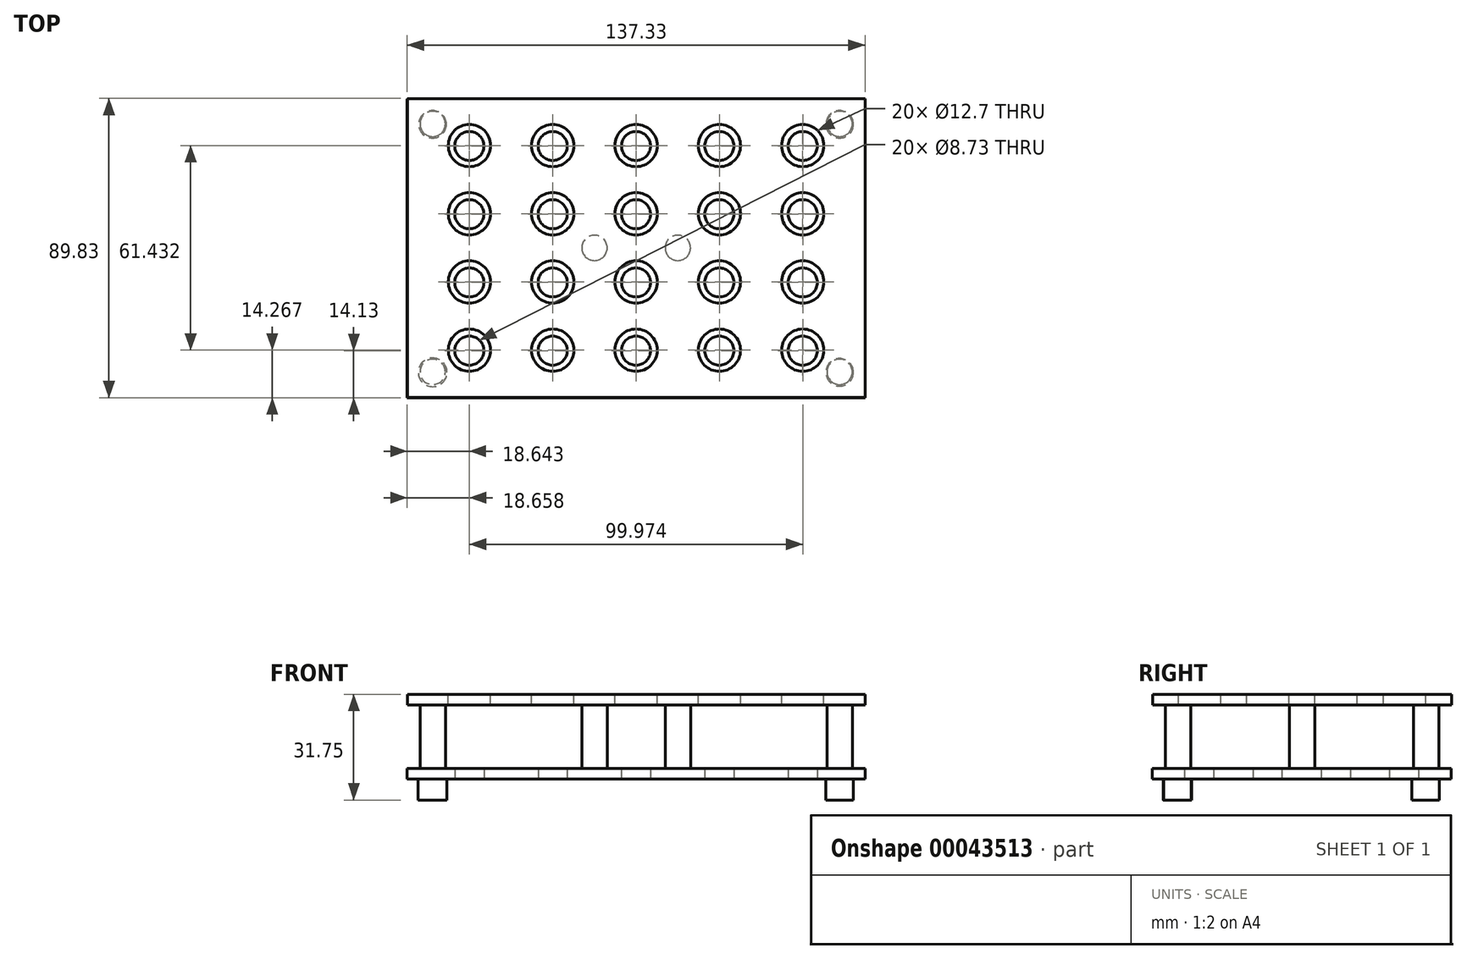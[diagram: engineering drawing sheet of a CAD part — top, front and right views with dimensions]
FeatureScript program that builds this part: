
annotation { "Feature Type Name" : "Feature", "Feature Type Description" : "" }
export const myFeature = defineFeature(function(context is Context, id is Id, definition is map)
    precondition{}
    {
        {
            var Q0;
            Q0=qCreatedBy(makeId("Top.planeOp"),FACE);
            var sketch = newSketch(context, id + "F0", { "sketchPlane" : qUnion([Q0])});
            skLineSegment(sketch, "E0.bottom", {"start": v(-64.77, 57.93) * mm, "end": v(72.55, 57.93) * mm});
            skLineSegment(sketch, "E0.top", {"start": v(-64.77, -31.76) * mm, "end": v(72.55, -31.76) * mm});
            skLineSegment(sketch, "E0.left", {"start": v(-64.77, 57.93) * mm, "end": v(-64.77, -31.76) * mm});
            skLineSegment(sketch, "E0.right", {"start": v(72.55, 57.93) * mm, "end": v(72.55, -31.76) * mm});
            skSolve(sketch);
        }
        {
            var Q0;
            Q0=makeQuery(id+"F0.imprint","IMPRINT",FACE,{"disambiguationData":[TD([[makeQuery(id+"F0.imprint","IMPRINT",EDGE,{"derivedFrom":sQuery(id+"F0.wireOp",EDGE,"E0.bottom")}),-1.0]])]});
            extrude(context, id + "F1", {"entities" : qUnion([Q0]), "oppositeDirection" : true, "depth" : 3.17 * mm});
        }
        {
            var Q0;
            Q0=makeQuery(id+"F1.opExtrude","CAP_FACE",FACE,{"disambiguationData":[OSD([sQuery(id+"F0.wireOp",EDGE,"E0.bottom"),sQuery(id+"F0.wireOp",EDGE,"E0.top"),sQuery(id+"F0.wireOp",EDGE,"E0.left"),sQuery(id+"F0.wireOp",EDGE,"E0.right")])],"isStart":true});
            var sketch = newSketch(context, id + "F2", { "sketchPlane" : qUnion([Q0])});
            skCircle(sketch, "E1", {"center": v(-46.12, 43.8) * mm, "radius": 6.35 * mm});
            skCircle(sketch, "E2", {"center": v(-21.13, 43.8) * mm, "radius": 6.35 * mm});
            skCircle(sketch, "E3", {"center": v(3.87, 43.8) * mm, "radius": 6.35 * mm});
            skCircle(sketch, "E4", {"center": v(28.86, 43.8) * mm, "radius": 6.35 * mm});
            skCircle(sketch, "E5", {"center": v(53.85, 43.8) * mm, "radius": 6.35 * mm});
            skCircle(sketch, "E6", {"center": v(-46.12, -17.63) * mm, "radius": 6.35 * mm});
            skCircle(sketch, "E7", {"center": v(-21.13, -17.63) * mm, "radius": 6.35 * mm});
            skCircle(sketch, "E8", {"center": v(3.87, -17.63) * mm, "radius": 6.35 * mm});
            skCircle(sketch, "E9", {"center": v(28.86, -17.63) * mm, "radius": 6.35 * mm});
            skCircle(sketch, "E10", {"center": v(53.85, -17.63) * mm, "radius": 6.35 * mm});
            skCircle(sketch, "E11", {"center": v(-46.12, 23.32) * mm, "radius": 6.35 * mm});
            skCircle(sketch, "E12", {"center": v(-21.13, 23.32) * mm, "radius": 6.35 * mm});
            skCircle(sketch, "E13", {"center": v(3.87, 23.32) * mm, "radius": 6.35 * mm});
            skCircle(sketch, "E14", {"center": v(28.86, 23.32) * mm, "radius": 6.35 * mm});
            skCircle(sketch, "E15", {"center": v(53.85, 23.32) * mm, "radius": 6.35 * mm});
            skCircle(sketch, "E16", {"center": v(-46.12, 2.85) * mm, "radius": 6.35 * mm});
            skCircle(sketch, "E17", {"center": v(-21.13, 2.85) * mm, "radius": 6.35 * mm});
            skCircle(sketch, "E18", {"center": v(3.87, 2.85) * mm, "radius": 6.35 * mm});
            skCircle(sketch, "E19", {"center": v(28.86, 2.85) * mm, "radius": 6.35 * mm});
            skCircle(sketch, "E20", {"center": v(53.85, 2.85) * mm, "radius": 6.35 * mm});
            skSolve(sketch);
        }
        {
            var Q0;
            Q0=makeQuery(id+"F1.opExtrude","CAP_FACE",FACE,{"disambiguationData":[OSD([sQuery(id+"F0.wireOp",EDGE,"E0.bottom"),sQuery(id+"F0.wireOp",EDGE,"E0.top"),sQuery(id+"F0.wireOp",EDGE,"E0.left"),sQuery(id+"F0.wireOp",EDGE,"E0.right")])],"isStart":false});
            var sketch = newSketch(context, id + "F3", { "sketchPlane" : qUnion([Q0])});
            skCircle(sketch, "E21", {"center": v(-57.15, 24.14) * mm, "radius": 3.81 * mm});
            skCircle(sketch, "E22", {"center": v(64.93, 24.14) * mm, "radius": 3.81 * mm});
            skCircle(sketch, "E23", {"center": v(-57.15, -50.3) * mm, "radius": 3.81 * mm});
            skCircle(sketch, "E24", {"center": v(64.93, -50.3) * mm, "radius": 3.81 * mm});
            skCircle(sketch, "E25", {"center": v(-8.6, -13.08) * mm, "radius": 3.81 * mm});
            skCircle(sketch, "E26", {"center": v(16.39, -13.08) * mm, "radius": 3.81 * mm});
            skSolve(sketch);
        }
        {
            var Q0;
            Q0 = qSketchRegion(id + "F3", true);
            extrude(context, id + "F4", {"entities" : qUnion([Q0]), "operationType" : NewBodyOperationType.ADD, "depth" : 19.05 * mm});
        }
        {
            var Q0;
            Q0=makeQuery(id+"F4.opExtrude","CAP_FACE",FACE,{"disambiguationData":[OSD([sQuery(id+"F3.wireOp",EDGE,"E26")])],"isStart":false});
            var sketch = newSketch(context, id + "F5", { "sketchPlane" : qUnion([Q0])});
            skLineSegment(sketch, "E27.bottom", {"start": v(-64.78, 31.9) * mm, "end": v(72.53, 31.9) * mm});
            skLineSegment(sketch, "E27.top", {"start": v(-64.78, -57.79) * mm, "end": v(72.53, -57.79) * mm});
            skLineSegment(sketch, "E27.left", {"start": v(-64.78, 31.9) * mm, "end": v(-64.78, -57.79) * mm});
            skLineSegment(sketch, "E27.right", {"start": v(72.53, 31.9) * mm, "end": v(72.53, -57.79) * mm});
            skSolve(sketch);
        }
        {
            var Q0;
            Q0 = qSketchRegion(id + "F5", true);
            extrude(context, id + "F6", {"entities" : qUnion([Q0]), "operationType" : NewBodyOperationType.ADD, "depth" : 3.17 * mm});
        }
        {
            var Q0;
            Q0=makeQuery(id+"F6.opExtrude","CAP_FACE",FACE,{"disambiguationData":[OSD([sQuery(id+"F5.wireOp",EDGE,"E27.bottom"),sQuery(id+"F5.wireOp",EDGE,"E27.top"),sQuery(id+"F5.wireOp",EDGE,"E27.left"),sQuery(id+"F5.wireOp",EDGE,"E27.right")])],"isStart":false});
            var sketch = newSketch(context, id + "F7", { "sketchPlane" : qUnion([Q0])});
            skLineSegment(sketch, "E28", {"start": v(-64.78, 24.12) * mm, "end": v(72.53, 24.12) * mm});
            skLineSegment(sketch, "E29", {"start": v(-64.78, 3.64) * mm, "end": v(72.53, 3.64) * mm});
            skLineSegment(sketch, "E30", {"start": v(-64.78, -16.83) * mm, "end": v(72.53, -16.83) * mm});
            skLineSegment(sketch, "E31", {"start": v(-64.78, -37.31) * mm, "end": v(72.53, -37.31) * mm});
            skCircle(sketch, "E32", {"center": v(-46.14, 17.77) * mm, "radius": 4.37 * mm});
            skCircle(sketch, "E33", {"center": v(-21.14, 17.77) * mm, "radius": 4.37 * mm});
            skCircle(sketch, "E34", {"center": v(3.85, 17.77) * mm, "radius": 4.37 * mm});
            skCircle(sketch, "E35", {"center": v(28.84, 17.77) * mm, "radius": 4.37 * mm});
            skCircle(sketch, "E36", {"center": v(53.84, 17.77) * mm, "radius": 4.37 * mm});
            skCircle(sketch, "E37", {"center": v(-46.14, -2.7) * mm, "radius": 4.37 * mm});
            skCircle(sketch, "E38", {"center": v(-21.14, -2.7) * mm, "radius": 4.37 * mm});
            skCircle(sketch, "E39", {"center": v(3.85, -2.7) * mm, "radius": 4.37 * mm});
            skCircle(sketch, "E40", {"center": v(28.84, -2.7) * mm, "radius": 4.37 * mm});
            skCircle(sketch, "E41", {"center": v(53.84, -2.7) * mm, "radius": 4.37 * mm});
            skCircle(sketch, "E42", {"center": v(-46.14, -23.18) * mm, "radius": 4.37 * mm});
            skCircle(sketch, "E43", {"center": v(-21.14, -23.18) * mm, "radius": 4.37 * mm});
            skCircle(sketch, "E44", {"center": v(3.85, -23.18) * mm, "radius": 4.37 * mm});
            skCircle(sketch, "E45", {"center": v(28.84, -23.18) * mm, "radius": 4.37 * mm});
            skCircle(sketch, "E46", {"center": v(53.84, -23.18) * mm, "radius": 4.37 * mm});
            skCircle(sketch, "E47", {"center": v(-46.14, -43.66) * mm, "radius": 4.37 * mm});
            skCircle(sketch, "E48", {"center": v(-21.14, -43.66) * mm, "radius": 4.37 * mm});
            skCircle(sketch, "E49", {"center": v(3.85, -43.66) * mm, "radius": 4.37 * mm});
            skCircle(sketch, "E50", {"center": v(28.84, -43.66) * mm, "radius": 4.37 * mm});
            skCircle(sketch, "E51", {"center": v(53.84, -43.66) * mm, "radius": 4.37 * mm});
            skSolve(sketch);
        }
        {
            var Q0;
            Q0 = qSketchRegion(id + "F2", true);
            extrude(context, id + "F8", {"entities" : qUnion([Q0]), "operationType" : NewBodyOperationType.REMOVE, "oppositeDirection" : true, "depth" : 6.35 * mm});
        }
        {
            var Q0;
            Q0 = qSketchRegion(id + "F7", true);
            extrude(context, id + "F9", {"entities" : qUnion([Q0]), "operationType" : NewBodyOperationType.REMOVE, "oppositeDirection" : true, "depth" : 25.4 * mm});
        }
        {
            var Q0;
            Q0=makeQuery(id+"F6.opExtrude","CAP_FACE",FACE,{"disambiguationData":[OSD([sQuery(id+"F5.wireOp",EDGE,"E27.bottom"),sQuery(id+"F5.wireOp",EDGE,"E27.top"),sQuery(id+"F5.wireOp",EDGE,"E27.left"),sQuery(id+"F5.wireOp",EDGE,"E27.right")])],"isStart":false});
            var sketch = newSketch(context, id + "F10", { "sketchPlane" : qUnion([Q0])});
            skCircle(sketch, "E52", {"center": v(-57.16, 24.28) * mm, "radius": 4.3 * mm});
            skCircle(sketch, "E53", {"center": v(64.91, 24.28) * mm, "radius": 4.13 * mm});
            skCircle(sketch, "E54", {"center": v(64.91, -50.17) * mm, "radius": 4.13 * mm});
            skCircle(sketch, "E55", {"center": v(-57.16, -50.17) * mm, "radius": 4.13 * mm});
            skSolve(sketch);
        }
        {
            var Q0;
            Q0 = qSketchRegion(id + "F10", true);
            extrude(context, id + "F11", {"entities" : qUnion([Q0]), "operationType" : NewBodyOperationType.ADD, "depth" : 6.35 * mm});
        }
    });
